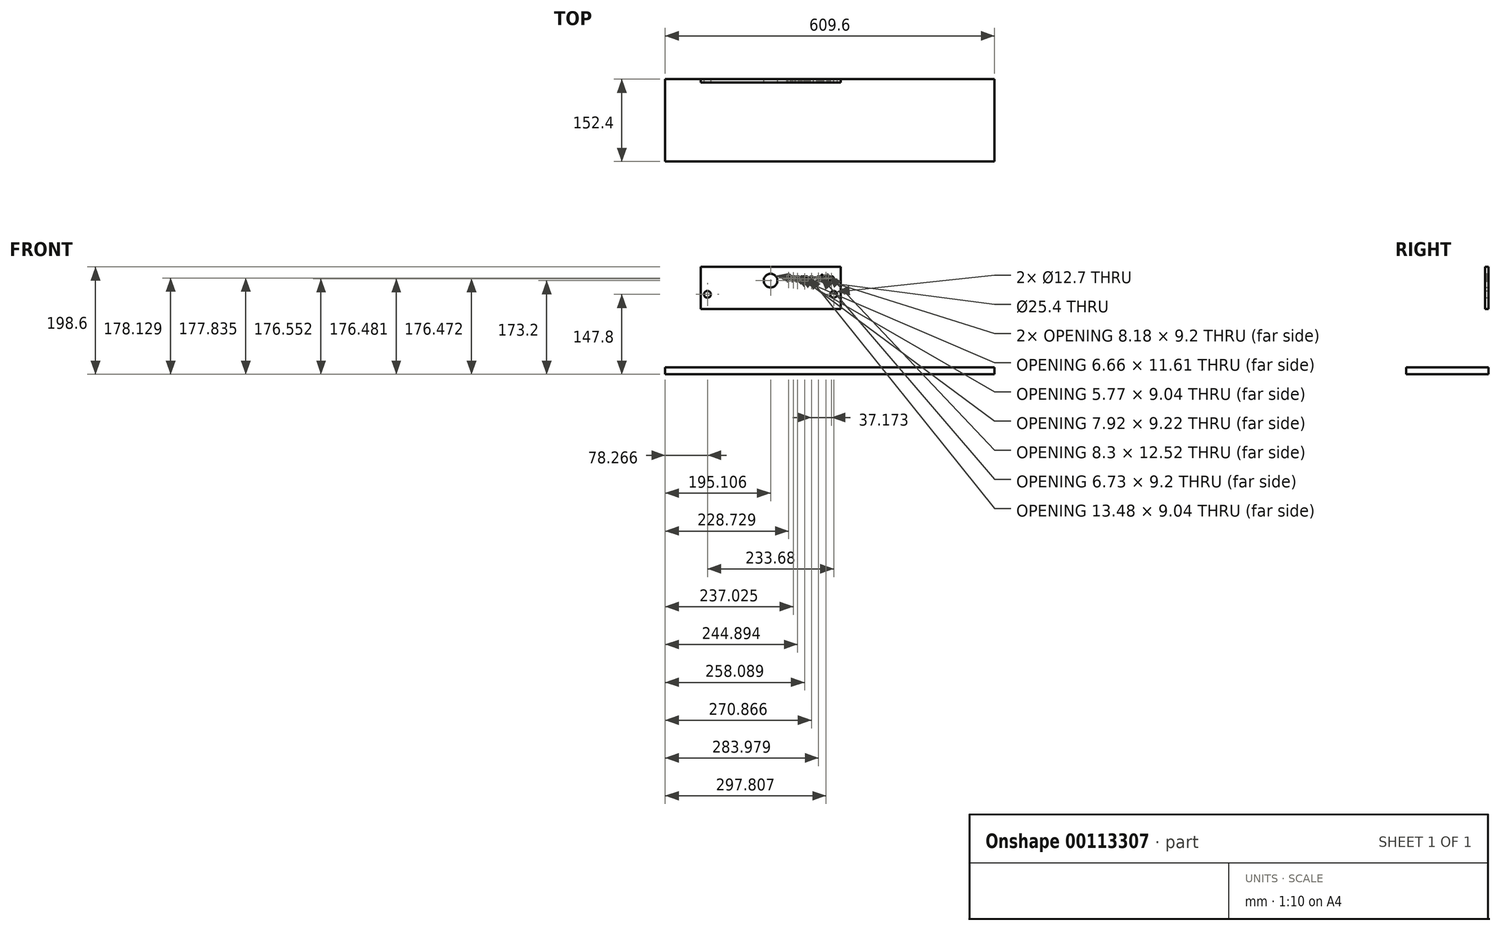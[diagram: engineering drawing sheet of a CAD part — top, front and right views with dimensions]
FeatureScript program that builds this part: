
annotation { "Feature Type Name" : "Feature", "Feature Type Description" : "" }
export const myFeature = defineFeature(function(context is Context, id is Id, definition is map)
    precondition{}
    {
        {
            var Q0;
            Q0=qCreatedBy(makeId("Front.planeOp"),FACE);
            var sketch = newSketch(context, id + "F0", { "sketchPlane" : qUnion([Q0])});
            skLineSegment(sketch, "E0.bottom", {"start": v(-94.17, 77.8) * mm, "end": v(164.9, 77.8) * mm});
            skLineSegment(sketch, "E0.top", {"start": v(-94.17, 0) * mm, "end": v(164.9, 0) * mm});
            skLineSegment(sketch, "E0.left", {"start": v(-94.17, 77.8) * mm, "end": v(-94.17, 0) * mm});
            skLineSegment(sketch, "E0.right", {"start": v(164.9, 77.8) * mm, "end": v(164.9, 0) * mm});
            skLineSegment(sketch, "E1", {"start": v(-81.47, 27) * mm, "end": v(152.2, 27) * mm, "construction": true});
            skLineSegment(sketch, "E2", {"start": v(35.37, 27) * mm, "end": v(35.37, 52.4) * mm, "construction": true});
            skText(sketch, "E3", { "text": "Frame side\n", "fontName": "OpenSans-Bold.ttf"});
            skCircle(sketch, "E4", {"center": v(-81.47, 27) * mm, "radius": 6.35 * mm});
            skCircle(sketch, "E5", {"center": v(152.2, 27) * mm, "radius": 6.35 * mm});
            skCircle(sketch, "E6", {"center": v(35.37, 52.4) * mm, "radius": 12.7 * mm});
            const initialGuessF0  = {"E3": [0.0642, 0.05123, 1, 0, 0.01171]};
            skSetInitialGuess(sketch, initialGuessF0);
            skSolve(sketch);
        }
        {
            var Q0;
            Q0=makeQuery(id+"F0.imprint","IMPRINT",FACE,{"disambiguationData":[TD([[makeQuery(id+"F0.imprint","IMPRINT",EDGE,{"derivedFrom":sQuery(id+"F0.wireOp",EDGE,"E0.bottom")}),-1.0]])]});
            extrude(context, id + "F1", {"entities" : qUnion([Q0]), "depth" : 6.35 * mm});
        }
        {
            var Q0;
            Q0=qCreatedBy(makeId("Front.planeOp"),FACE);
            var sketch = newSketch(context, id + "F2", { "sketchPlane" : qUnion([Q0])});
            skLineSegment(sketch, "E7.bottom", {"start": v(-159.74, -108.1) * mm, "end": v(449.86, -108.1) * mm});
            skLineSegment(sketch, "E7.top", {"start": v(-159.74, -120.8) * mm, "end": v(449.86, -120.8) * mm});
            skLineSegment(sketch, "E7.left", {"start": v(-159.74, -108.1) * mm, "end": v(-159.74, -120.8) * mm});
            skLineSegment(sketch, "E7.right", {"start": v(449.86, -108.1) * mm, "end": v(449.86, -120.8) * mm});
            skSolve(sketch);
        }
        {
            var Q0;
            Q0=makeQuery(id+"F2.imprint","IMPRINT",FACE,{"disambiguationData":[TD([[makeQuery(id+"F2.imprint","IMPRINT",EDGE,{"derivedFrom":sQuery(id+"F2.wireOp",EDGE,"E7.bottom")}),-1.0]])]});
            extrude(context, id + "F3", {"entities" : qUnion([Q0]), "depth" : 152.4 * mm});
        }
    });
